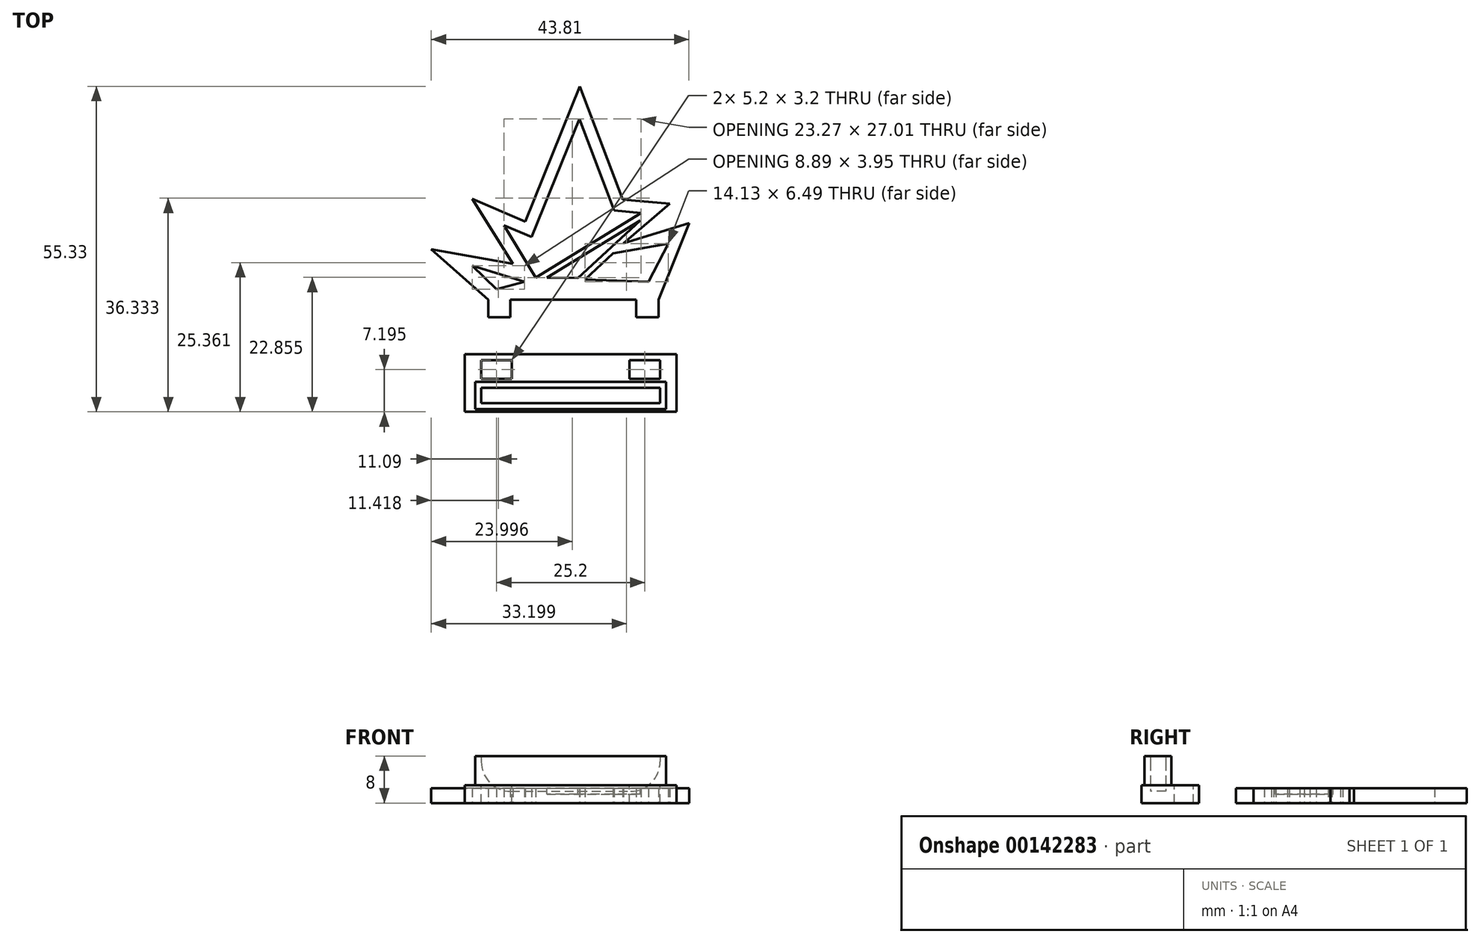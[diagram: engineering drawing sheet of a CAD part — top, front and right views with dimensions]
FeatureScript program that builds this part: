
annotation { "Feature Type Name" : "Feature", "Feature Type Description" : "" }
export const myFeature = defineFeature(function(context is Context, id is Id, definition is map)
    precondition{}
    {
        {
            var Q0;
            Q0=qCreatedBy(makeId("Top.planeOp"),FACE);
            var sketch = newSketch(context, id + "F0", { "sketchPlane" : qUnion([Q0])});
            skLineSegment(sketch, "E0", {"start": v(-14.04, 0) * mm, "end": v(14.96, 0) * mm});
            skLineSegment(sketch, "E1", {"start": v(-14.04, 0) * mm, "end": v(-23.7, 8.61) * mm});
            skLineSegment(sketch, "E2", {"start": v(-23.7, 8.61) * mm, "end": v(-9.82, 6.08) * mm});
            skLineSegment(sketch, "E3", {"start": v(-9.82, 6.08) * mm, "end": v(-16.75, 17.16) * mm});
            skLineSegment(sketch, "E4", {"start": v(-16.75, 17.16) * mm, "end": v(-7.73, 13.3) * mm});
            skLineSegment(sketch, "E5", {"start": v(-7.73, 13.3) * mm, "end": v(1.54, 36.27) * mm});
            skLineSegment(sketch, "E6", {"start": v(1.54, 36.27) * mm, "end": v(8.83, 17.04) * mm});
            skLineSegment(sketch, "E7", {"start": v(8.83, 17.04) * mm, "end": v(16.83, 16.3) * mm});
            skLineSegment(sketch, "E8", {"start": v(16.83, 16.3) * mm, "end": v(9, 9.6) * mm});
            skLineSegment(sketch, "E9", {"start": v(9, 9.6) * mm, "end": v(20.12, 13.05) * mm});
            skLineSegment(sketch, "E10", {"start": v(20.12, 13.05) * mm, "end": v(14.96, 0) * mm});
            skLineSegment(sketch, "E11.0", {"start": v(-11.33, 12.66) * mm, "end": v(-6.64, 10.66) * mm});
            skLineSegment(sketch, "E11.2", {"start": v(1.48, 30.78) * mm, "end": v(7.4, 15.16) * mm});
            skLineSegment(sketch, "E11.3", {"start": v(7.4, 15.16) * mm, "end": v(11.94, 14.75) * mm});
            skLineSegment(sketch, "E11.5", {"start": v(-6.64, 10.66) * mm, "end": v(1.48, 30.78) * mm});
            skLineSegment(sketch, "E12.bottom", {"start": v(-14.04, 0) * mm, "end": v(-10.24, 0) * mm});
            skLineSegment(sketch, "E12.top", {"start": v(-14.04, -3) * mm, "end": v(-10.24, -3) * mm});
            skLineSegment(sketch, "E12.left", {"start": v(-14.04, 0) * mm, "end": v(-14.04, -3) * mm});
            skLineSegment(sketch, "E12.right", {"start": v(-10.24, 0) * mm, "end": v(-10.24, -3) * mm});
            skLineSegment(sketch, "E13.bottom", {"start": v(14.96, 0) * mm, "end": v(11.16, 0) * mm});
            skLineSegment(sketch, "E13.top", {"start": v(14.96, -3) * mm, "end": v(11.16, -3) * mm});
            skLineSegment(sketch, "E13.left", {"start": v(14.96, 0) * mm, "end": v(14.96, -3) * mm});
            skLineSegment(sketch, "E13.right", {"start": v(11.16, 0) * mm, "end": v(11.16, -3) * mm});
            skLineSegment(sketch, "E14", {"start": v(-11.33, 12.66) * mm, "end": v(-5.92, 3.77) * mm});
            skLineSegment(sketch, "E15", {"start": v(-5.92, 3.77) * mm, "end": v(11.94, 14.75) * mm});
            skLineSegment(sketch, "E16", {"start": v(7.22, 7.88) * mm, "end": v(2.45, 3.44) * mm});
            skLineSegment(sketch, "E17", {"start": v(2.45, 3.44) * mm, "end": v(13.23, 3.05) * mm});
            skLineSegment(sketch, "E18", {"start": v(13.23, 3.05) * mm, "end": v(16.57, 9.55) * mm});
            skLineSegment(sketch, "E19", {"start": v(16.57, 9.55) * mm, "end": v(7.22, 7.88) * mm});
            skLineSegment(sketch, "E20", {"start": v(-7.83, 3.04) * mm, "end": v(-16.72, 5.77) * mm});
            skLineSegment(sketch, "E21", {"start": v(-16.72, 5.77) * mm, "end": v(-12.61, 1.82) * mm});
            skLineSegment(sketch, "E22", {"start": v(-12.61, 1.82) * mm, "end": v(-7.83, 3.04) * mm});
            skLineSegment(sketch, "E23", {"start": v(-14.04, 0) * mm, "end": v(-10.24, -3) * mm, "construction": true});
            skLineSegment(sketch, "E24", {"start": v(-14.04, -3) * mm, "end": v(-10.24, 0) * mm, "construction": true});
            skLineSegment(sketch, "E25", {"start": v(11.16, 0) * mm, "end": v(14.96, -3) * mm, "construction": true});
            skLineSegment(sketch, "E26", {"start": v(11.16, -3) * mm, "end": v(14.96, 0) * mm, "construction": true});
            skPoint(sketch, "E27", {"position": v(-12.14, -1.5) * mm});
            skPoint(sketch, "E28", {"position": v(13.06, -1.5) * mm});
            skSolve(sketch);
        }
        {
            var Q0;
            Q0 = qSketchRegion(id + "F0", true);
            extrude(context, id + "F1", {"entities" : qUnion([Q0]), "depth" : 2.5 * mm});
        }
        {
            var Q0;
            Q0=qCreatedBy(makeId("Top.planeOp"),FACE);
            var sketch = newSketch(context, id + "F2", { "sketchPlane" : qUnion([Q0])});
            skLineSegment(sketch, "E29.bottom", {"start": v(-18, -9.26) * mm, "end": v(18, -9.26) * mm});
            skLineSegment(sketch, "E29.top", {"start": v(-18, -19.06) * mm, "end": v(18, -19.06) * mm});
            skLineSegment(sketch, "E29.left", {"start": v(-18, -9.26) * mm, "end": v(-18, -19.06) * mm});
            skLineSegment(sketch, "E29.right", {"start": v(18, -9.26) * mm, "end": v(18, -19.06) * mm});
            skSolve(sketch);
        }
        {
            var Q0;
            Q0=makeQuery(id+"F2.imprint","IMPRINT",FACE,{"disambiguationData":[TD([[makeQuery(id+"F2.imprint","IMPRINT",EDGE,{"derivedFrom":sQuery(id+"F2.wireOp",EDGE,"E29.bottom")}),-1.0]])]});
            extrude(context, id + "F3", {"entities" : qUnion([Q0]), "depth" : 3 * mm});
        }
        {
            var Q0;
            Q0=makeQuery(id+"F3.opExtrude","CAP_FACE",FACE,{"disambiguationData":[OSD([sQuery(id+"F2.wireOp",EDGE,"E29.bottom"),sQuery(id+"F2.wireOp",EDGE,"E29.top"),sQuery(id+"F2.wireOp",EDGE,"E29.left"),sQuery(id+"F2.wireOp",EDGE,"E29.right")])],"isStart":false});
            var sketch = newSketch(context, id + "F4", { "sketchPlane" : qUnion([Q0])});
            skLineSegment(sketch, "E30.bottom", {"start": v(-15.2, -10.26) * mm, "end": v(-10, -10.26) * mm});
            skLineSegment(sketch, "E30.top", {"start": v(-15.2, -13.46) * mm, "end": v(-10, -13.46) * mm});
            skLineSegment(sketch, "E30.left", {"start": v(-15.2, -10.26) * mm, "end": v(-15.2, -13.46) * mm});
            skLineSegment(sketch, "E30.right", {"start": v(-10, -10.26) * mm, "end": v(-10, -13.46) * mm});
            skLineSegment(sketch, "E31.MirrorCS", {"start": v(10, -10.26) * mm, "end": v(10, -13.46) * mm});
            skLineSegment(sketch, "E32.MirrorCS", {"start": v(15.2, -10.26) * mm, "end": v(10, -10.26) * mm});
            skLineSegment(sketch, "E33.MirrorCS", {"start": v(15.2, -10.26) * mm, "end": v(15.2, -13.46) * mm});
            skLineSegment(sketch, "E34.MirrorCS", {"start": v(15.2, -13.46) * mm, "end": v(10, -13.46) * mm});
            skLineSegment(sketch, "E35", {"start": v(-10, -10.26) * mm, "end": v(-15.2, -13.46) * mm, "construction": true});
            skLineSegment(sketch, "E36", {"start": v(10, -10.26) * mm, "end": v(15.2, -13.46) * mm, "construction": true});
            skLineSegment(sketch, "E37", {"start": v(15.2, -10.26) * mm, "end": v(10, -13.46) * mm, "construction": true});
            skLineSegment(sketch, "E38", {"start": v(-15.2, -10.26) * mm, "end": v(-10, -13.46) * mm, "construction": true});
            skPoint(sketch, "E39", {"position": v(-12.6, -11.86) * mm});
            skPoint(sketch, "E40", {"position": v(12.6, -11.86) * mm});
            skSolve(sketch);
        }
        {
            var Q0;
            Q0 = qSketchRegion(id + "F4", true);
            extrude(context, id + "F5", {"entities" : qUnion([Q0]), "operationType" : NewBodyOperationType.REMOVE, "oppositeDirection" : true, "depth" : 25 * mm});
        }
        {
            var Q0;
            Q0=makeQuery(id+"F3.opExtrude","CAP_FACE",FACE,{"disambiguationData":[OSD([sQuery(id+"F2.wireOp",EDGE,"E29.bottom"),sQuery(id+"F2.wireOp",EDGE,"E29.top"),sQuery(id+"F2.wireOp",EDGE,"E29.left"),sQuery(id+"F2.wireOp",EDGE,"E29.right")])],"isStart":false});
            var sketch = newSketch(context, id + "F6", { "sketchPlane" : qUnion([Q0])});
            skLineSegment(sketch, "E41.bottom", {"start": v(-15.2, -14.96) * mm, "end": v(15.2, -14.96) * mm});
            skLineSegment(sketch, "E41.top", {"start": v(-15.2, -17.56) * mm, "end": v(15.2, -17.56) * mm});
            skLineSegment(sketch, "E41.left", {"start": v(-15.2, -14.96) * mm, "end": v(-15.2, -17.56) * mm});
            skLineSegment(sketch, "E41.right", {"start": v(15.2, -14.96) * mm, "end": v(15.2, -17.56) * mm});
            skLineSegment(sketch, "E42.0", {"start": v(-16.2, -13.96) * mm, "end": v(16.2, -13.96) * mm});
            skLineSegment(sketch, "E42.1", {"start": v(-16.2, -13.96) * mm, "end": v(-16.2, -18.56) * mm});
            skLineSegment(sketch, "E42.2", {"start": v(-16.2, -18.56) * mm, "end": v(16.2, -18.56) * mm});
            skLineSegment(sketch, "E42.3", {"start": v(16.2, -13.96) * mm, "end": v(16.2, -18.56) * mm});
            skSolve(sketch);
        }
        {
            var Q0;
            Q0=makeQuery(id+"F6.imprint","IMPRINT",FACE,{"disambiguationData":[TD([[makeQuery(id+"F6.imprint","IMPRINT",EDGE,{"derivedFrom":sQuery(id+"F6.wireOp",EDGE,"E41.bottom")}),1.0]])]});
            extrude(context, id + "F7", {"entities" : qUnion([Q0]), "operationType" : NewBodyOperationType.ADD, "depth" : 5 * mm});
        }
        {
            var Q0;
            Q0=makeQuery(id+"F6.imprint","IMPRINT",FACE,{"disambiguationData":[TD([[makeQuery(id+"F6.imprint","IMPRINT",EDGE,{"derivedFrom":sQuery(id+"F6.wireOp",EDGE,"E41.bottom")}),-1.0]])]});
            extrude(context, id + "F8", {"entities" : qUnion([Q0]), "operationType" : NewBodyOperationType.REMOVE, "oppositeDirection" : true, "depth" : 1 * mm});
        }
        {
            var Q0;
            Q0=makeQuery(id+"F8.boolean.opBoolean","COPY",EDGE,{"derivedFrom":makeQuery(id+"F8.opExtrude","CAP_EDGE",EDGE,{"disambiguationData":[OSD([sQuery(id+"F6.wireOp",EDGE,"E41.left")])],"isStart":false})});
            var Q1;
            Q1=makeQuery(id+"F8.boolean.opBoolean","COPY",EDGE,{"derivedFrom":makeQuery(id+"F8.opExtrude","CAP_EDGE",EDGE,{"disambiguationData":[OSD([sQuery(id+"F6.wireOp",EDGE,"E41.right")])],"isStart":false})});
            fillet(context, id + "F9", {"entities" : qUnion([Q0, Q1]), "radius" : 5 * mm, "tangentPropagation" : true, "allowEdgeOverflow" : false});
        }
        {
            var Q0;
            Q0=makeQuery(id+"F1.opExtrude","CAP_FACE",FACE,{"disambiguationData":[OSD([sQuery(id+"F0.wireOp",EDGE,"E0"),sQuery(id+"F0.wireOp",EDGE,"E1"),sQuery(id+"F0.wireOp",EDGE,"E2"),sQuery(id+"F0.wireOp",EDGE,"E3"),sQuery(id+"F0.wireOp",EDGE,"E4"),sQuery(id+"F0.wireOp",EDGE,"E5"),sQuery(id+"F0.wireOp",EDGE,"E6"),sQuery(id+"F0.wireOp",EDGE,"E7"),sQuery(id+"F0.wireOp",EDGE,"E8"),sQuery(id+"F0.wireOp",EDGE,"E9"),sQuery(id+"F0.wireOp",EDGE,"E10"),sQuery(id+"F0.wireOp",EDGE,"E11.0"),sQuery(id+"F0.wireOp",EDGE,"E11.2"),sQuery(id+"F0.wireOp",EDGE,"E11.3"),sQuery(id+"F0.wireOp",EDGE,"E11.5"),sQuery(id+"F0.wireOp",EDGE,"E12.top"),sQuery(id+"F0.wireOp",EDGE,"E12.left"),sQuery(id+"F0.wireOp",EDGE,"E12.right"),sQuery(id+"F0.wireOp",EDGE,"E13.top"),sQuery(id+"F0.wireOp",EDGE,"E13.left"),sQuery(id+"F0.wireOp",EDGE,"E13.right"),sQuery(id+"F0.wireOp",EDGE,"E14"),sQuery(id+"F0.wireOp",EDGE,"E15"),sQuery(id+"F0.wireOp",EDGE,"E16"),sQuery(id+"F0.wireOp",EDGE,"E17"),sQuery(id+"F0.wireOp",EDGE,"E18"),sQuery(id+"F0.wireOp",EDGE,"E19"),sQuery(id+"F0.wireOp",EDGE,"E20"),sQuery(id+"F0.wireOp",EDGE,"E21"),sQuery(id+"F0.wireOp",EDGE,"E22")])],"isStart":false});
            var sketch = newSketch(context, id + "F10", { "sketchPlane" : qUnion([Q0])});
            skLineSegment(sketch, "E43.0", {"start": v(-4.06, 3.74) * mm, "end": v(11.82, 13.5) * mm});
            skLineSegment(sketch, "E44.0", {"start": v(11.82, 13.5) * mm, "end": v(1.22, 3.67) * mm});
            skLineSegment(sketch, "E45", {"start": v(1.22, 3.67) * mm, "end": v(-4.06, 3.74) * mm});
            skSolve(sketch);
        }
        {
            var Q0;
            Q0 = qSketchRegion(id + "F10", true);
            extrude(context, id + "F11", {"entities" : qUnion([Q0]), "operationType" : NewBodyOperationType.REMOVE, "oppositeDirection" : true, "depth" : 1 * mm});
        }
    });
